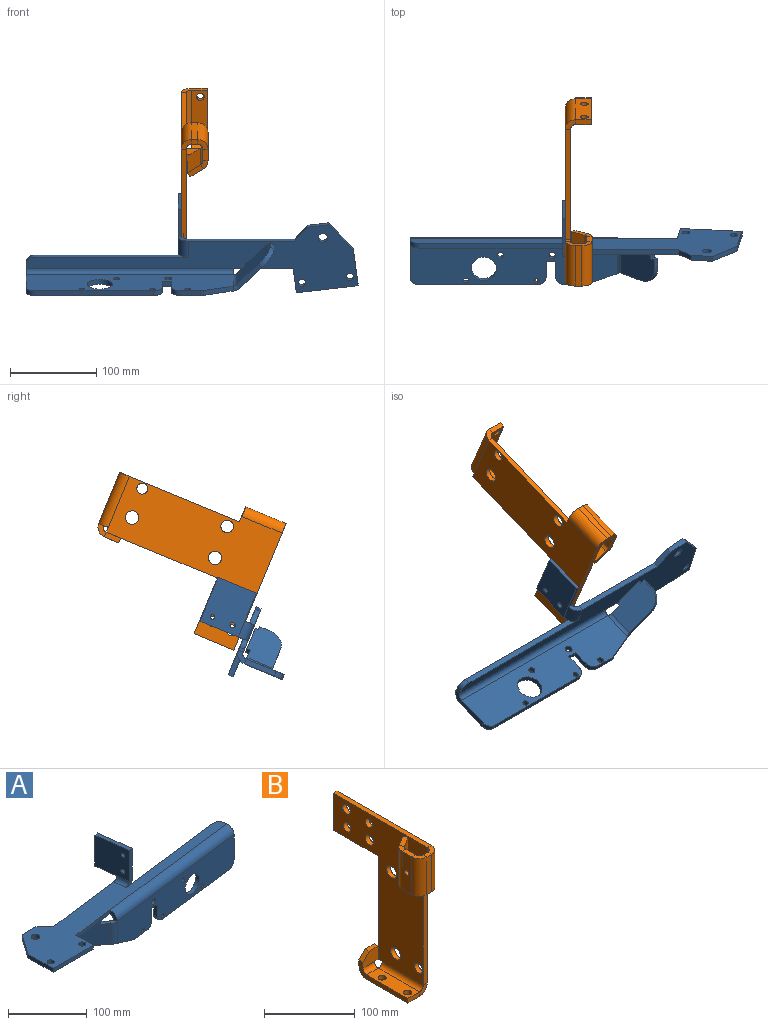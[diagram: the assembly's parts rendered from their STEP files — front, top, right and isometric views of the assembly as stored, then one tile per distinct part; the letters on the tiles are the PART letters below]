
ASSEMBLY  parts=2 mates=1
PART A: 66 faces, bbox 380.9x115.8x114 mm
  f0: plane 69.15x8.49mm, normal (0.12,-0.99,0), area 418mm2, adj f8,f13,f14,f63
  f1: plane 45x6mm, normal (-1,0,0), area 270mm2, adj f2,f9,f13,f14
  f2: plane 35x24.41mm, normal (-0.82,0.57,0), area 256mm2, adj f1,f3,f13,f14
  f3: plane 25x6mm, normal (0,1,0), area 150mm2, adj f2,f4,f13,f14
  f4: plane 16.6x15.43mm, normal (0.68,0.73,0), area 136mm2, adj f3,f5,f13,f14
  f5: plane 122.4x15.03mm, normal (-0.12,0.99,0), area 739.9mm2, adj f4,f13,f14,f24
  f6: plane 176.95x21.73mm, normal (-0.12,0.99,0), area 1025.5mm2, adj f13,f14,f15,f26
  f7: plane 6x3.97mm, normal (0.99,0.12,0), area 24mm2, adj f13,f14,f15,f62
  f8: plane 31.05x6mm, normal (1,0,0), area 186.3mm2, adj f0,f9,f13,f14
  f9: plane 72x6mm, normal (0,-1,0), area 432mm2, adj f1,f8,f13,f14
  f10: cylinder r=4.5mm len=9mm, axis (0,0,1), area 169.6mm2, adj f13,f14
  f11: cylinder r=4.5mm len=9mm, axis (0,0,1), area 169.6mm2, adj f13,f14
  f12: cylinder r=5.5mm len=11mm, axis (0,0,1), area 207.3mm2, adj f13,f14
  f13: plane 379.43x81.54mm, normal (0,0,-1), area 11565.5mm2, adj f0,f1,f2,f3,f4,f5,f6,f7
  f14: plane 379.43x81.54mm, normal (0,0,1), area 11565.5mm2, adj f0,f1,f2,f3,f4,f5,f6,f7
  f15: cylinder r=10mm len=11.14mm, axis (0,0,1), area 94.2mm2, adj f6,f7,f13,f14
  f16: plane 35.47x10.22mm, normal (0,0,-1), area 210mm2, adj f17,f22,f23,f24
  f17: plane 48x5.96mm, normal (-0.12,0.99,0), area 288mm2, adj f16,f18,f22,f23
  f18: plane 55.32x12.66mm, normal (0,0,1), area 330mm2, adj f17,f19,f22,f23
  f19: plane 48x5.96mm, normal (0.12,-0.99,0), area 288mm2, adj f18,f22,f23,f25
  f20: cylinder r=2.67mm len=6.61mm, axis (0.99,0.12,0), area 100.8mm2, adj f22,f23
  f21: cylinder r=3.05mm len=6.79mm, axis (0.99,0.12,0), area 115.2mm2, adj f22,f23
  f22: plane 54.59x48mm, normal (0.99,0.12,0), area 2588.2mm2, adj f16,f17,f18,f19,f20,f21,f26
  f23: plane 54.59x48mm, normal (-0.99,-0.12,0), area 2588.2mm2, adj f16,f17,f18,f19,f20,f21,f27
  f24: plane 12x11.91mm, normal (-0.12,0.99,0), area 84.8mm2, adj f5,f16,f26,f27
  f25: plane 11.91x6mm, normal (0.12,-0.99,0), area 40.6mm2, adj f14,f19,f26,f27
  f26: cylinder r=12mm len=21.31mm, axis (-0.12,0.99,0), area 377mm2, adj f6,f13,f22,f24,f25
  f27: cylinder r=6mm len=20.58mm, axis (-0.12,0.99,0), area 188.5mm2, adj f14,f23,f24,f25
  f28: plane 5.96x0.73mm, normal (-0.99,-0.12,0), area 2.8mm2, adj f42,f43,f58,f63
  f29: plane 38x5.96mm, normal (0.99,0.12,0), area 228mm2, adj f42,f43,f44,f62
  f30: plane 137.57x22.76mm, normal (0,0,-1), area 827.2mm2, adj f42,f43,f44,f45
  f31: plane 18.5x5.96mm, normal (-0.99,-0.12,0), area 111mm2, adj f32,f42,f43,f45
  f32: plane 11.77x7.31mm, normal (0,0,-1), area 66.7mm2, adj f31,f33,f42,f43
  f33: plane 18.5x5.96mm, normal (0.99,0.12,0), area 111mm2, adj f32,f42,f43,f46
  f34: plane 24.05x8.82mm, normal (0,0,-1), area 140.9mm2, adj f42,f43,f46,f47
  f35: cylinder r=3.58mm len=7.83mm, axis (-0.12,0.99,0), area 134.8mm2, adj f42,f43
  f36: cylinder r=3.08mm len=6.84mm, axis (-0.12,0.99,0), area 115.9mm2, adj f42,f43
  f37: cylinder r=14.63mm len=29.77mm, axis (-0.12,0.99,0), area 551.5mm2, adj f42,f43
  f38: cylinder r=2.96mm len=6.68mm, axis (-0.12,0.99,0), area 111.6mm2, adj f42,f43
  f39: cylinder r=3.33mm len=7.33mm, axis (-0.12,0.99,0), area 125.4mm2, adj f42,f43
  f40: cylinder r=4.12mm len=8.9mm, axis (-0.12,0.99,0), area 155.1mm2, adj f42,f43
  f41: plane 34.54x12.84mm, normal (-0.35,-0.04,-0.94), area 218.4mm2, adj f42,f43,f47,f59
  f42: plane 238.28x48mm, normal (-0.12,0.99,0), area 10043mm2, adj f28,f29,f30,f31,f32,f33,f34,f35
  f43: plane 238.28x48mm, normal (0.12,-0.99,0), area 10043mm2, adj f28,f29,f30,f31,f32,f33,f34,f35
  f44: cylinder r=10mm len=10.66mm, axis (-0.12,0.99,0), area 94.2mm2, adj f29,f30,f42,f43
  f45: cylinder r=10mm len=10.66mm, axis (0.12,-0.99,0), area 94.2mm2, adj f30,f31,f42,f43
  f46: cylinder r=10mm len=10.66mm, axis (0.12,-0.99,0), area 94.2mm2, adj f33,f34,f42,f43
  f47: cylinder r=10mm len=6.39mm, axis (0.12,-0.99,0), area 21.6mm2, adj f34,f41,f42,f43
  f48: plane 12.17x4.73mm, normal (-0.79,0.62,0), area 73mm2, adj f49,f55,f56,f57
  f49: plane 8.18x8.11mm, normal (0,0,1), area 33.6mm2, adj f48,f50,f55,f56
  f50: plane 4.73x3.91mm, normal (-0.79,0.62,0), area 23.5mm2, adj f49,f51,f55,f56
  f51: plane 32.07x26.9mm, normal (0,0,1), area 216.1mm2, adj f50,f52,f55,f56
  f52: plane 4.73x3.91mm, normal (0.79,-0.62,0), area 23.5mm2, adj f51,f53,f55,f56
  f53: plane 14.26x12.99mm, normal (0,0,1), area 80.5mm2, adj f52,f55,f56,f58
  f54: plane 31.3x26.29mm, normal (0,0,-1), area 210.2mm2, adj f55,f56,f57,f59
  f55: plane 43.36x36.08mm, normal (0.62,0.79,0), area 1825.3mm2, adj f48,f49,f50,f51,f52,f53,f54,f57
  f56: plane 43.36x36.08mm, normal (-0.62,-0.79,0), area 1825.3mm2, adj f48,f49,f50,f51,f52,f53,f54,f57
  f57: cylinder r=20mm len=20mm, axis (0.62,0.79,0), area 188.5mm2, adj f48,f54,f55,f56
  f58: plane 8.85x7.27mm, normal (0,0,1), area 42.4mm2, adj f28,f53,f60,f61
  f59: bspline ~8.85x7.3mm, area 44.4mm2, adj f41,f54,f60,f61
  f60: cylinder r=12mm len=34.05mm, axis (0,0,1), area 309.2mm2, adj f43,f56,f58,f59
  f61: cylinder r=6mm len=34.05mm, axis (0,0,1), area 154.6mm2, adj f42,f55,f58,f59
  f62: plane 12x11.91mm, normal (0.99,0.12,0), area 84.8mm2, adj f7,f29,f64,f65
  f63: plane 12x11.91mm, normal (-0.99,-0.12,0), area 84.8mm2, adj f0,f28,f64,f65
  f64: cylinder r=12mm len=239.75mm, axis (0.99,0.12,0), area 4525.3mm2, adj f14,f43,f62,f63
  f65: cylinder r=6mm len=239.01mm, axis (0.99,0.12,0), area 2262.6mm2, adj f13,f42,f62,f63
PART B: 65 faces, bbox 31x158.8x200.8 mm
  f0: plane 121.06x6mm, normal (0,1,0), area 726.4mm2, adj f1,f7,f16,f17
  f1: plane 18x6mm, normal (0,1,0), area 108mm2, adj f0,f2,f16,f17
  f2: plane 6x5.98mm, normal (0,0,-1), area 35.9mm2, adj f1,f16,f17,f35
  f3: plane 138.17x6mm, normal (0,-1,0), area 829mm2, adj f4,f16,f17,f36
  f4: plane 6.84x6mm, normal (0,0,-1), area 41mm2, adj f3,f16,f17,f61
  f5: plane 146.78x6mm, normal (0,0,1), area 880.7mm2, adj f6,f16,f17,f62
  f6: plane 49.7x6mm, normal (0,1,0), area 298.2mm2, adj f5,f7,f16,f17
  f7: plane 69.96x6mm, normal (0,0,-1), area 419.8mm2, adj f0,f6,f16,f17
  f8: cylinder r=7.28mm len=14.57mm, axis (1,0,0), area 274.6mm2, adj f16,f17
  f9: cylinder r=7.69mm len=15.38mm, axis (1,0,0), area 289.9mm2, adj f16,f17
  f10: cylinder r=6.26mm len=12.51mm, axis (1,0,0), area 235.9mm2, adj f16,f17
  f11: cylinder r=7.76mm len=15.52mm, axis (1,0,0), area 292.6mm2, adj f16,f17
  f12: cylinder r=5.62mm len=11.23mm, axis (1,0,0), area 211.7mm2, adj f16,f17
  f13: cylinder r=6.26mm len=12.51mm, axis (1,0,0), area 235.9mm2, adj f16,f17
  f14: cylinder r=6.34mm len=12.69mm, axis (1,0,0), area 239.1mm2, adj f16,f17
  f15: cylinder r=5.9mm len=11.8mm, axis (1,0,0), area 222.4mm2, adj f16,f17
  f16: plane 188.76x146.78mm, normal (-1,0,0), area 15910.2mm2, adj f0,f1,f2,f3,f4,f5,f6,f7
  f17: plane 188.76x146.78mm, normal (1,0,0), area 15910.2mm2, adj f0,f1,f2,f3,f4,f5,f6,f7
  f18: plane 64x6mm, normal (-1,0,0), area 384mm2, adj f19,f22,f23,f31
  f19: plane 18x6mm, normal (0,-1,0), area 108mm2, adj f18,f22,f23,f36
  f20: cylinder r=4.5mm len=9mm, axis (0,0,1), area 169.6mm2, adj f22,f23
  f21: cylinder r=4.5mm len=9mm, axis (0,0,1), area 169.6mm2, adj f22,f23
  f22: plane 64x18mm, normal (0,0,1), area 1024.8mm2, adj f18,f19,f20,f21,f34,f38
  f23: plane 64x18mm, normal (0,0,-1), area 1024.8mm2, adj f18,f19,f20,f21,f33,f37
  f24: plane 6x5.98mm, normal (0,0,-1), area 35.9mm2, adj f27,f28,f29,f32
  f25: plane 13.98x6mm, normal (0,0,1), area 83.9mm2, adj f27,f28,f29,f30
  f26: plane 8x6mm, normal (-1,0,0), area 48mm2, adj f28,f29,f30,f31
  f27: plane 18x6mm, normal (1,0,0), area 108mm2, adj f24,f25,f28,f29
  f28: plane 23.98x18mm, normal (0,-1,0), area 381.6mm2, adj f24,f25,f26,f27,f30,f34
  f29: plane 23.98x18mm, normal (0,1,0), area 381.6mm2, adj f24,f25,f26,f27,f30,f33
  f30: plane 10x10mm, normal (-0.71,0,0.71), area 84.9mm2, adj f25,f26,f28,f29
  f31: plane 12x12mm, normal (-1,0,0), area 84.8mm2, adj f18,f26,f33,f34
  f32: plane 12x12mm, normal (1,0,0), area 84.8mm2, adj f24,f33,f34,f35
  f33: cylinder r=12mm len=18mm, axis (-1,0,0), area 339.3mm2, adj f23,f29,f31,f32
  f34: cylinder r=6mm len=18mm, axis (-1,0,0), area 169.6mm2, adj f22,f28,f31,f32
  f35: plane 12x12mm, normal (0,1,0), area 84.8mm2, adj f2,f32,f37,f38
  f36: plane 12x12mm, normal (0,-1,0), area 84.8mm2, adj f3,f19,f37,f38
  f37: cylinder r=12mm len=64mm, axis (0,1,0), area 1206.4mm2, adj f17,f23,f35,f36
  f38: cylinder r=6mm len=64mm, axis (0,1,0), area 603.2mm2, adj f16,f22,f35,f36
  f39: plane 7x6mm, normal (0,0,1), area 42mm2, adj f41,f42,f57,f62
  f40: plane 7x6mm, normal (0,0,-1), area 42mm2, adj f41,f42,f58,f61
  f41: plane 50.59x7mm, normal (0,1,0), area 354.1mm2, adj f39,f40,f60,f64
  f42: plane 50.59x7mm, normal (0,-1,0), area 354.1mm2, adj f39,f40,f59,f63
  f43: plane 14.74x6mm, normal (0,0,1), area 88.5mm2, adj f46,f47,f53,f57
  f44: cylinder r=3.4mm len=6.8mm, axis (1,0,0), area 128.2mm2, adj f46,f47
  f45: plane 14.74x6mm, normal (0,0,-1), area 88.5mm2, adj f46,f47,f54,f58
  f46: plane 50.59x14.74mm, normal (1,0,0), area 709.5mm2, adj f43,f44,f45,f56,f60
  f47: plane 50.59x14.74mm, normal (-1,0,0), area 709.5mm2, adj f43,f44,f45,f55,f59
  f48: plane 50.59x5.03mm, normal (0.84,0.54,0), area 303.6mm2, adj f49,f50,f51,f52
  f49: plane 18.77x15.1mm, normal (0,0,1), area 110.9mm2, adj f48,f51,f52,f53
  f50: plane 18.77x15.1mm, normal (0,0,-1), area 110.9mm2, adj f48,f51,f52,f54
  f51: plane 50.59x15.5mm, normal (0.54,-0.84,0), area 935.2mm2, adj f48,f49,f50,f56
  f52: plane 50.59x15.5mm, normal (-0.54,0.84,0), area 935.2mm2, adj f48,f49,f50,f55
  f53: plane 10.06x8.73mm, normal (0,0,1), area 53.7mm2, adj f43,f49,f55,f56
  f54: plane 10.06x8.73mm, normal (0,0,-1), area 53.7mm2, adj f45,f50,f55,f56
  f55: cylinder r=12mm len=50.59mm, axis (0,0,1), area 604mm2, adj f47,f52,f53,f54
  f56: cylinder r=6mm len=50.59mm, axis (0,0,1), area 302mm2, adj f46,f51,f53,f54
  f57: plane 12x12mm, normal (0,0,1), area 84.8mm2, adj f39,f43,f59,f60
  f58: plane 12x12mm, normal (0,0,-1), area 84.8mm2, adj f40,f45,f59,f60
  f59: cylinder r=12mm len=50.59mm, axis (0,0,1), area 953.6mm2, adj f42,f47,f57,f58
  f60: cylinder r=6mm len=50.59mm, axis (0,0,1), area 476.8mm2, adj f41,f46,f57,f58
  f61: plane 12x12mm, normal (0,0,-1), area 84.8mm2, adj f4,f40,f63,f64
  f62: plane 12x12mm, normal (0,0,1), area 84.8mm2, adj f5,f39,f63,f64
  f63: cylinder r=12mm len=50.59mm, axis (0,0,-1), area 953.6mm2, adj f17,f42,f61,f62
  f64: cylinder r=6mm len=50.59mm, axis (0,0,-1), area 476.8mm2, adj f16,f41,f61,f62
PLACE A rot(axis=(-0.03,0.56,0.83),174.2deg) t=(115.98,-122.99,-202.5)mm
PLACE B rot(axis=(0,-0.83,0.56),180deg) t=(33.81,-72.64,-78.21)mm
MATE parallel A.f22 <-> B.f16  axis (-1,0,0) through (23.98,-121.71,-111.23)mm
